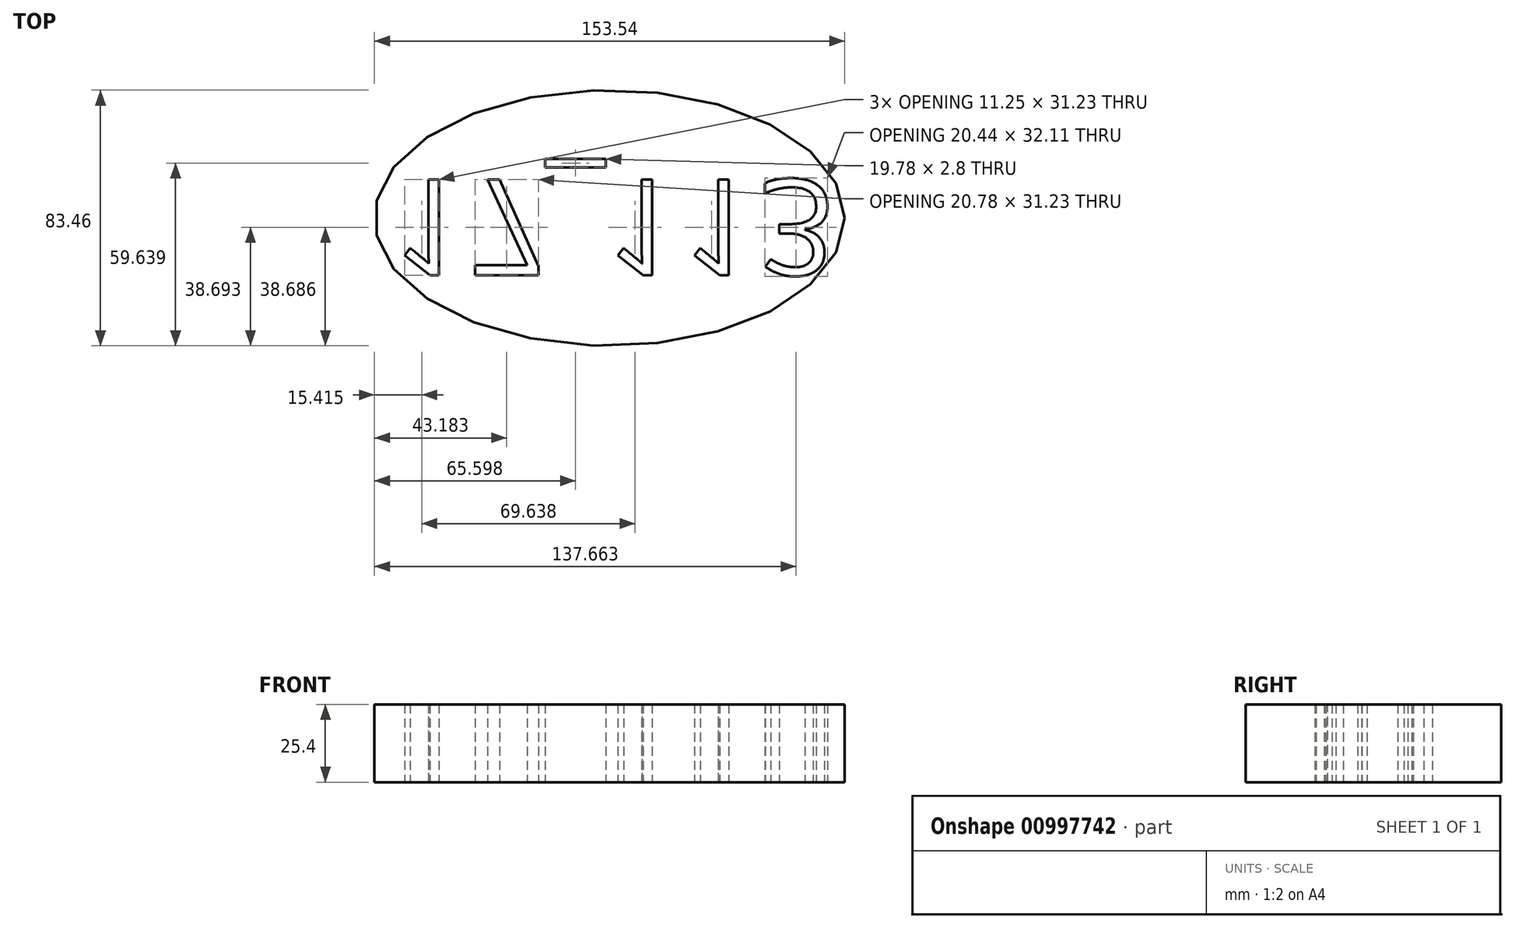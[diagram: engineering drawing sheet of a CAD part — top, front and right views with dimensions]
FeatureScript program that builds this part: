
annotation { "Feature Type Name" : "Feature", "Feature Type Description" : "" }
export const myFeature = defineFeature(function(context is Context, id is Id, definition is map)
    precondition{}
    {
        {
            var Q0;
            Q0=qCreatedBy(makeId("Top.planeOp"),FACE);
            var sketch = newSketch(context, id + "F0", { "sketchPlane" : qUnion([Q0])});
            skEllipse(sketch, "E0", {"center": v(0, 0) * mm, "majorRadius": 76.77 * mm, "minorRadius": 41.73 * mm, "majorAxis": v(1, 0)});
            skSolve(sketch);
        }
        {
            var Q0;
            Q0=makeQuery(id+"F0.imprint","IMPRINT",FACE,{"disambiguationData":[TD([[makeQuery(id+"F0.imprint","IMPRINT",EDGE,{"derivedFrom":sQuery(id+"F0.wireOp",EDGE,"E0")}),1.0]])]});
            extrude(context, id + "F1", {"entities" : qUnion([Q0]), "depth" : 25.4 * mm, "offsetDistance" : 25.4 * mm});
        }
        {
            var Q0;
            Q0=makeQuery(id+"F1.opExtrude","CAP_FACE",FACE,{"disambiguationData":[OSD([sQuery(id+"F0.wireOp",EDGE,"E0")])],"isStart":true});
            var sketch = newSketch(context, id + "F2", { "sketchPlane" : qUnion([Q0])});
            skText(sketch, "E1", { "text": "17_113", "fontName": "OpenSans-Regular.ttf"});
            const initialGuessF2  = {"E1": [-0.071, -0.01258, 1, 0, 0.0315]};
            skSetInitialGuess(sketch, initialGuessF2);
            skSolve(sketch);
        }
        {
            var Q0;
            Q0 = qSketchRegion(id + "F2", true);
            extrude(context, id + "F3", {"entities" : qUnion([Q0]), "operationType" : NewBodyOperationType.REMOVE, "oppositeDirection" : true, "depth" : 25.4 * mm, "offsetDistance" : 25.4 * mm});
        }
    });
